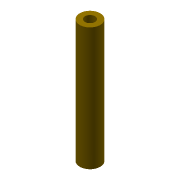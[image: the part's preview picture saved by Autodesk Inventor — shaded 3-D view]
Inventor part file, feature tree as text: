
AUTODESK INVENTOR PART (.ipt)
format: ipt  version: 2022 (Build 260153000, 153)  size: 114,176 bytes
history: native  units: mm
features: sketch x2, extrude x1, hole x1
ambient origin geometry x8: Origin, YZ Plane, XZ Plane, XY Plane, X Axis, Y Axis, Z Axis, Center Point
bodies: Solid1 (feature_tree)
feature tree (4):
  extrude  "Extrusion1"  Depth=30.0mm TaperAngle=0.0deg
  hole  "Hole1"  [1 undecoded]
  sketch  "Sketch1"  dims[d0=5.0mm d1=30.0mm d2=0.0mm]
  sketch  "Sketch2"  dims[d3=2.459mm d4=10.0mm d5=4.0mm d6=2.0mm d7=90.0deg d8=8.0mm d9=20.594885mm]
note: 1 required parameter value undecoded (feature->parameter linkage not recoverable at this tier; creation-order binding heuristic only, values carry confidence <= 0.55)
